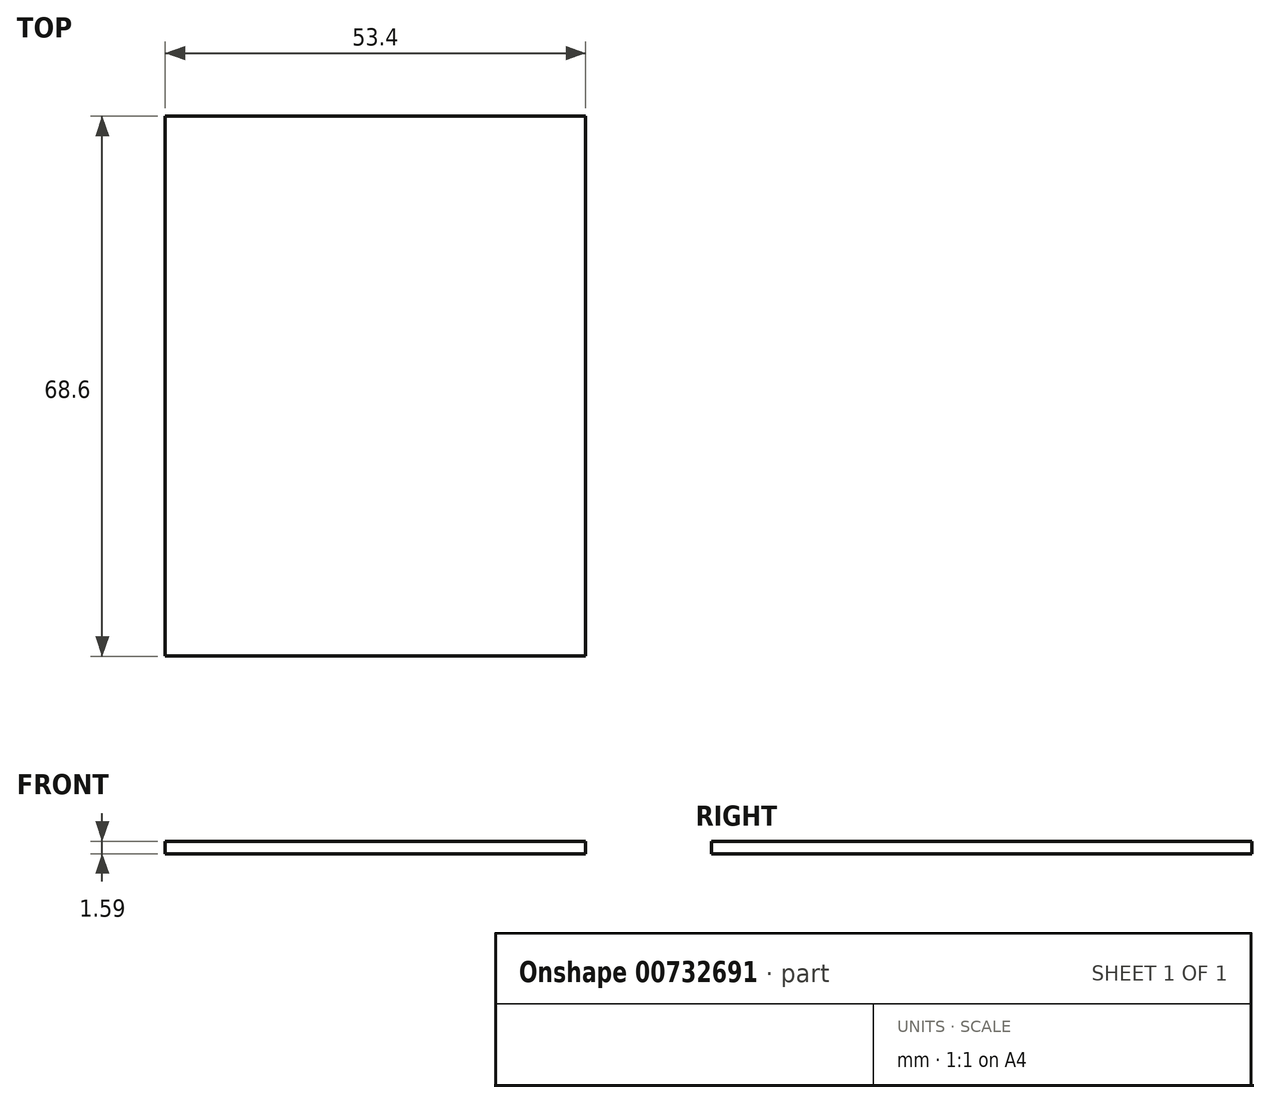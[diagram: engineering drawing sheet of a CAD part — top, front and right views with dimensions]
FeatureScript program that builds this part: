
annotation { "Feature Type Name" : "Feature", "Feature Type Description" : "" }
export const myFeature = defineFeature(function(context is Context, id is Id, definition is map)
    precondition{}
    {
        {
            var Q0;
            Q0=qCreatedBy(makeId("Top.planeOp"),FACE);
            var sketch = newSketch(context, id + "F0", { "sketchPlane" : qUnion([Q0])});
            skLineSegment(sketch, "E0.bottom", {"start": v(-10.3, 48.66) * mm, "end": v(43.1, 48.66) * mm});
            skLineSegment(sketch, "E0.top", {"start": v(-10.3, -19.94) * mm, "end": v(43.1, -19.94) * mm});
            skLineSegment(sketch, "E0.left", {"start": v(-10.3, 48.66) * mm, "end": v(-10.3, -19.94) * mm});
            skLineSegment(sketch, "E0.right", {"start": v(43.1, 48.66) * mm, "end": v(43.1, -19.94) * mm});
            skSolve(sketch);
        }
        {
            var Q0;
            Q0=makeQuery(id+"F0.imprint","IMPRINT",FACE,{"disambiguationData":[TD([[makeQuery(id+"F0.imprint","IMPRINT",EDGE,{"derivedFrom":sQuery(id+"F0.wireOp",EDGE,"E0.bottom")}),-1.0]])]});
            extrude(context, id + "F1", {"entities" : qUnion([Q0]), "depth" : 1.59 * mm, "offsetDistance" : 25.4 * mm});
        }
    });
